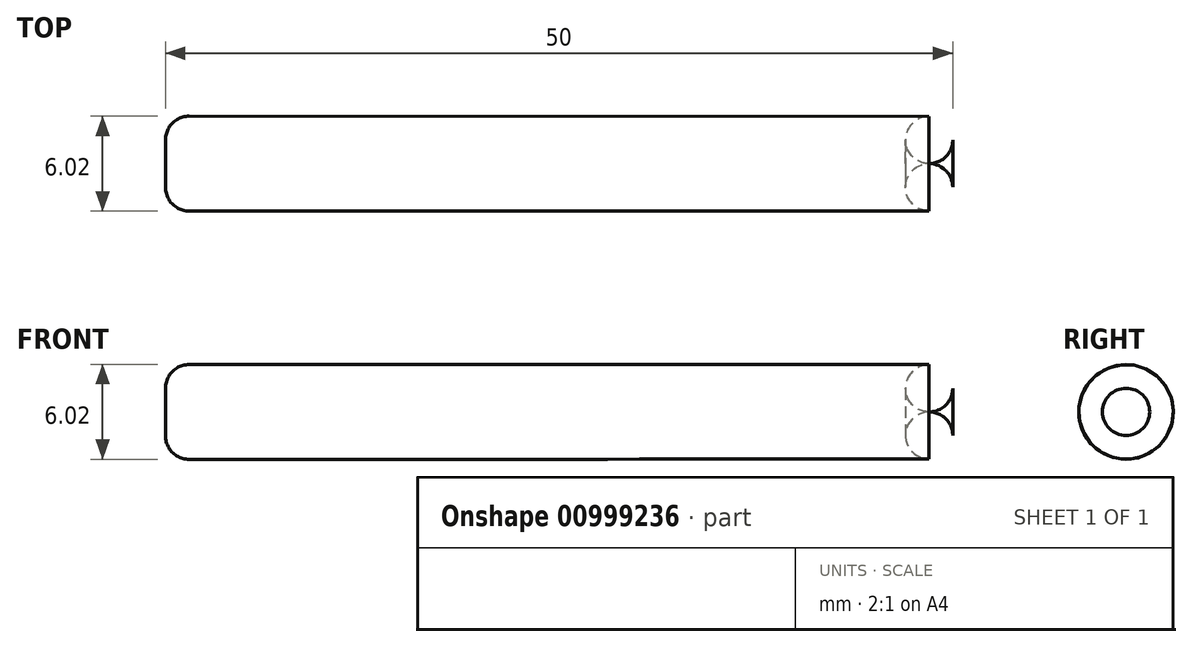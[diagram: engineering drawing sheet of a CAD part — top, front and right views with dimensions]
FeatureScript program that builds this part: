
annotation { "Feature Type Name" : "Feature", "Feature Type Description" : "" }
export const myFeature = defineFeature(function(context is Context, id is Id, definition is map)
    precondition{}
    {
        {
            var Q0;
            Q0=qCreatedBy(makeId("Front.planeOp"),FACE);
            var sketch = newSketch(context, id + "F0", { "sketchPlane" : qUnion([Q0])});
            skLineSegment(sketch, "E0.top", {"start": v(25.75, -1.5) * mm, "end": v(-24.25, -1.5) * mm});
            skPoint(sketch, "E0.middle", {"position": v(0, 0) * mm});
            skLineSegment(sketch, "E1", {"start": v(-24.25, -1.5) * mm, "end": v(-24.25, 0) * mm});
            skLineSegment(sketch, "E2", {"start": v(24.25, 1.5) * mm, "end": v(-22.75, 1.5) * mm});
            skArc(sketch, "E3", {"start": v(-22.75, 1.5) * mm, "mid": v(-23.81, 1.07) * mm, "end": v(-24.25, 0) * mm});
            skLineSegment(sketch, "E4", {"start": v(25.75, -1.5) * mm, "end": v(25.75, 0) * mm});
            skArc(sketch, "E5", {"start": v(25.75, 0) * mm, "mid": v(25.31, 1.06) * mm, "end": v(24.25, 1.5) * mm});
            skSolve(sketch);
        }
        {
            var Q0;
            Q0=qSketchRegion(id+"F0",true);
            var Q1;
            Q1=sQuery(id+"F0.wireOp",EDGE,"E0.top");
            revolve(context, id + "F1", {"surfaceOperationType" : NewSurfaceOperationType.NEW, "entities" : qUnion([Q0]), "axis" : qUnion([Q1]), "revolveType" : RevolveType.FULL});
        }
    });
